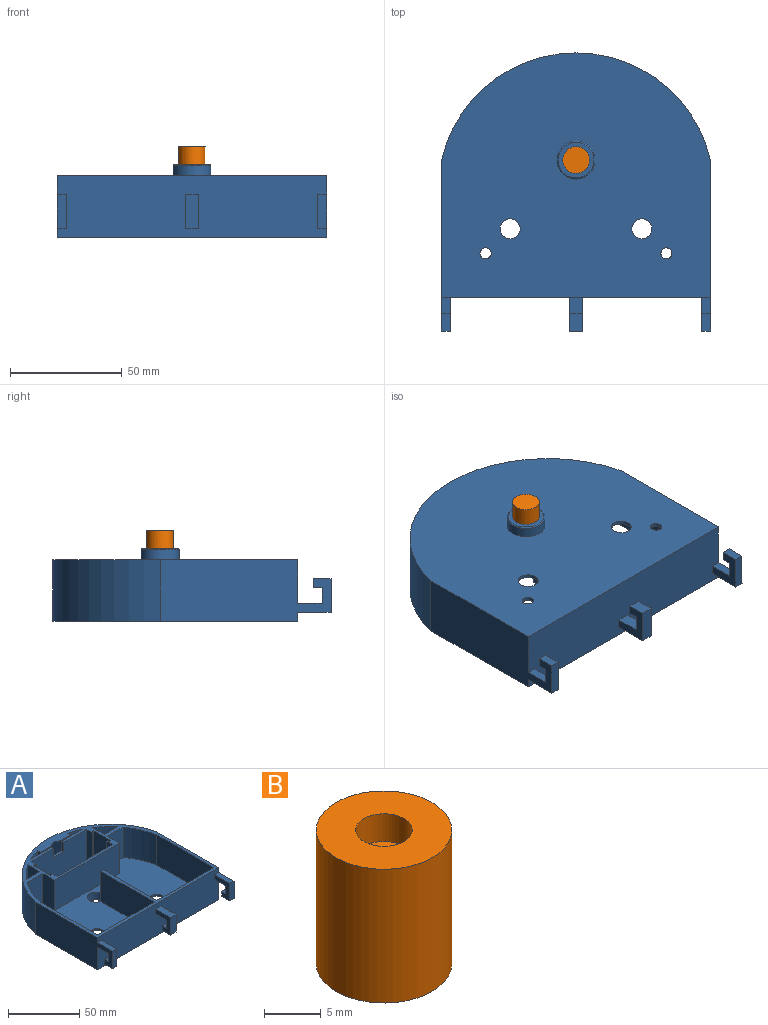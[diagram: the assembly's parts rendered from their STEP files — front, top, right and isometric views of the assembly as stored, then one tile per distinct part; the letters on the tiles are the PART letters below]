
ASSEMBLY  parts=2 mates=1
PART A: 95 faces, bbox 120.5x124.6x32.5 mm
  f0: plane 120.5x109.55mm, normal (0,0,1), area 1790.4mm2, adj f1,f2,f3,f5,f6,f8,f9,f12
  f1: plane 55x26mm, normal (0,-1,0), area 1350mm2, adj f0,f3,f4,f5,f6,f7,f85
  f2: plane 55x26mm, normal (0,1,0), area 1430mm2, adj f0,f3,f4,f85
  f3: plane 26x26mm, normal (1,0,0), area 359.2mm2, adj f0,f1,f2,f4,f76,f77,f78
  f4: plane 55x26mm, normal (0,0,1), area 1430mm2, adj f1,f2,f3,f85
  f5: plane 8x2mm, normal (1,0,0), area 16mm2, adj f0,f1,f7,f68
  f6: plane 8x2mm, normal (-1,0,0), area 16mm2, adj f0,f1,f7,f68
  f7: plane 10x2mm, normal (0,0,1), area 20mm2, adj f1,f5,f6,f68
  f8: cylinder r=58.84mm len=26mm, axis (0,0,1), area 462.6mm2, adj f0,f11,f13,f73
  f9: cylinder r=58.84mm len=26mm, axis (0,0,1), area 462.6mm2, adj f0,f10,f12,f74
  f10: plane 13.25x11.77mm, normal (0,0,1), area 85.9mm2, adj f9,f12,f74
  f11: plane 13.25x11.77mm, normal (0,0,1), area 85.9mm2, adj f8,f13,f73
  f12: plane 26x11.77mm, normal (-1,0,0), area 306mm2, adj f0,f9,f10,f74
  f13: plane 26x11.77mm, normal (1,0,0), area 306mm2, adj f0,f8,f11,f73
  f14: cylinder r=58.84mm len=51.77mm, axis (0,0,1), area 817.5mm2, adj f0,f16,f57,f58,f60,f68
  f15: cylinder r=58.84mm len=26mm, axis (0,0,1), area 666.6mm2, adj f0,f39,f54,f72
  f16: plane 51.77x6mm, normal (0,0,1), area 209.3mm2, adj f14,f68
  f17: cylinder r=58.84mm len=26mm, axis (0,0,1), area 666.6mm2, adj f0,f39,f40,f75
  f18: plane 53.18x26mm, normal (1,0,0), area 1382.7mm2, adj f0,f39,f55,f67
  f19: cylinder r=4.5mm len=9mm, axis (0,0,1), area 42.4mm2, adj f22,f39
  f20: plane 76.5x27.5mm, normal (-1,0,0), area 1811.2mm2, adj f0,f21,f22,f31,f32,f33,f35,f36
  f21: plane 120.5x27.5mm, normal (0,-1,0), area 3259.7mm2, adj f0,f20,f22,f25,f29,f30,f34,f37
  f22: plane 120.5x109.55mm, normal (0,0,-1), area 11331.1mm2, adj f19,f20,f21,f43,f44,f56,f64,f84
  f23: plane 7x5.5mm, normal (0,1,0), area 38.5mm2, adj f25,f28,f30,f45
  f24: plane 5.5x4mm, normal (0,1,0), area 22mm2, adj f25,f27,f28,f45
  f25: plane 15x15mm, normal (-1,0,0), area 120mm2, adj f21,f23,f24,f26,f27,f28,f29,f30
  f26: plane 15x5.5mm, normal (0,-1,0), area 82.5mm2, adj f25,f27,f29,f45
  f27: plane 8x5.5mm, normal (0,0,-1), area 44mm2, adj f24,f25,f26,f45
  f28: plane 5.5x4mm, normal (0,0,1), area 22mm2, adj f23,f24,f25,f45
  f29: plane 15x5.5mm, normal (0,0,1), area 82.5mm2, adj f21,f25,f26,f45
  f30: plane 11x5.5mm, normal (0,0,-1), area 60.5mm2, adj f21,f23,f25,f45
  f31: plane 7x4mm, normal (0,1,0), area 28mm2, adj f20,f34,f36,f38
  f32: plane 4x4mm, normal (0,1,0), area 16mm2, adj f20,f34,f35,f36
  f33: plane 15x4mm, normal (0,-1,0), area 60mm2, adj f20,f34,f35,f37
  f34: plane 15x15mm, normal (1,0,0), area 120mm2, adj f21,f31,f32,f33,f35,f36,f37,f38
  f35: plane 8x4mm, normal (0,0,-1), area 32mm2, adj f20,f32,f33,f34
  f36: plane 4x4mm, normal (0,0,1), area 16mm2, adj f20,f31,f32,f34
  f37: plane 15x4mm, normal (0,0,1), area 60mm2, adj f20,f21,f33,f34
  f38: plane 11x4mm, normal (0,0,-1), area 44mm2, adj f20,f21,f31,f34
  f39: plane 115.5x79.82mm, normal (0,0,1), area 7863.9mm2, adj f15,f17,f18,f19,f40,f41,f42,f43
  f40: plane 56.5x26mm, normal (1,0,0), area 1469mm2, adj f0,f17,f39,f41
  f41: plane 56.5x26mm, normal (0,1,0), area 1469mm2, adj f0,f39,f40,f42
  f42: plane 53.18x26mm, normal (-1,0,0), area 1382.7mm2, adj f0,f39,f41,f67
  f43: cylinder r=4.5mm len=9mm, axis (0,0,1), area 42.4mm2, adj f22,f39
  f44: plane 76.5x27.5mm, normal (1,0,0), area 1811.2mm2, adj f0,f21,f22,f46,f47,f48,f50,f51
  f45: plane 15x15mm, normal (1,0,0), area 120mm2, adj f21,f23,f24,f26,f27,f28,f29,f30
  f46: plane 7x4mm, normal (0,1,0), area 28mm2, adj f44,f49,f51,f53
  f47: plane 4x4mm, normal (0,1,0), area 16mm2, adj f44,f49,f50,f51
  f48: plane 15x4mm, normal (0,-1,0), area 60mm2, adj f44,f49,f50,f52
  f49: plane 15x15mm, normal (-1,0,0), area 120mm2, adj f21,f46,f47,f48,f50,f51,f52,f53
  f50: plane 8x4mm, normal (0,0,-1), area 32mm2, adj f44,f47,f48,f49
  f51: plane 4x4mm, normal (0,0,1), area 16mm2, adj f44,f46,f47,f49
  f52: plane 15x4mm, normal (0,0,1), area 60mm2, adj f21,f44,f48,f49
  f53: plane 11x4mm, normal (0,0,-1), area 44mm2, adj f21,f44,f46,f49
  f54: plane 56.5x26mm, normal (-1,0,0), area 1469mm2, adj f0,f15,f39,f55
  f55: plane 56.5x26mm, normal (0,1,0), area 1469mm2, adj f0,f18,f39,f54
  f56: cylinder r=61.8mm len=120.5mm, axis (0,0,1), area 4576.5mm2, adj f0,f20,f22,f44
  f57: plane 30x5mm, normal (0,0,-1), area 130.7mm2, adj f14,f58,f59,f60
  f58: plane 19x3.06mm, normal (-1,0,0), area 58.1mm2, adj f0,f14,f57,f59
  f59: plane 30x19mm, normal (0,-1,0), area 285.2mm2, adj f0,f57,f58,f60,f61,f62,f63
  f60: plane 19x3.06mm, normal (1,0,0), area 58.1mm2, adj f0,f14,f57,f59
  f61: plane 15x13.99mm, normal (-0.43,-0.86,-0.26), area 164.8mm2, adj f0,f59,f62,f63
  f62: plane 15x13.99mm, normal (0.43,-0.86,-0.26), area 164.8mm2, adj f0,f59,f61,f63
  f63: plane 27.97x6.99mm, normal (0,0,1), area 97.8mm2, adj f59,f61,f62
  f64: cylinder r=8.5mm len=17mm, axis (0,0,1), area 240.3mm2, adj f22,f66
  f65: plane 16x16mm, normal (0,0,-1), area 88mm2, adj f66,f67
  f66: torus R=8mm, axis (0,0,1), area 41mm2, adj f64,f65
  f67: cylinder r=6mm len=32.5mm, axis (0,0,1), area 310.5mm2, adj f0,f18,f39,f42,f65
  f68: plane 51.77x26mm, normal (0,1,0), area 1266.1mm2, adj f0,f5,f6,f7,f14,f16
  f69: plane 26x11.77mm, normal (-1,0,0), area 306mm2, adj f0,f39,f70,f75
  f70: plane 64x26mm, normal (0,-1,0), area 1664mm2, adj f0,f39,f69,f71
  f71: plane 26x11.77mm, normal (1,0,0), area 306mm2, adj f0,f39,f70,f72
  f72: plane 26x15.59mm, normal (0,-1,0), area 405.3mm2, adj f0,f15,f39,f71
  f73: plane 26x13.25mm, normal (0,1,0), area 344.6mm2, adj f0,f8,f11,f13
  f74: plane 26x13.25mm, normal (0,1,0), area 344.6mm2, adj f0,f9,f10,f12
  f75: plane 26x15.59mm, normal (0,-1,0), area 405.3mm2, adj f0,f17,f39,f69
  f76: plane 22x1.4mm, normal (0,-1,0), area 30.8mm2, adj f0,f3,f78,f82
  f77: plane 22x1.4mm, normal (0,1,0), area 30.8mm2, adj f0,f3,f78,f81
  f78: plane 17x2.5mm, normal (0,0,1), area 38.9mm2, adj f3,f76,f77,f79,f80,f81,f82,f83
  f79: plane 22x17mm, normal (1,0,0), area 374mm2, adj f0,f78,f80,f83
  f80: plane 22x1.1mm, normal (0,1,0), area 24.2mm2, adj f0,f78,f79,f81
  f81: plane 22x1.3mm, normal (-1,0,0), area 28.6mm2, adj f0,f77,f78,f80
  f82: plane 22x1.3mm, normal (-1,0,0), area 28.6mm2, adj f0,f76,f78,f83
  f83: plane 22x1.1mm, normal (0,-1,0), area 24.2mm2, adj f0,f78,f79,f82
  f84: cylinder r=2.5mm len=5mm, axis (0,0,1), area 23.6mm2, adj f22,f39
  f85: plane 26x26mm, normal (-1,0,0), area 359.2mm2, adj f0,f1,f2,f4,f86,f87,f89
  f86: plane 22x1.4mm, normal (0,-1,0), area 30.8mm2, adj f0,f85,f89,f93
  f87: plane 22x1.4mm, normal (0,1,0), area 30.8mm2, adj f0,f85,f89,f91
  f88: plane 22x17mm, normal (-1,0,0), area 374mm2, adj f0,f89,f90,f92
  f89: plane 17x2.5mm, normal (0,0,1), area 38.9mm2, adj f85,f86,f87,f88,f90,f91,f92,f93
  f90: plane 22x1.1mm, normal (0,1,0), area 24.2mm2, adj f0,f88,f89,f91
  f91: plane 22x1.3mm, normal (1,0,0), area 28.6mm2, adj f0,f87,f89,f90
  f92: plane 22x1.1mm, normal (0,-1,0), area 24.2mm2, adj f0,f88,f89,f93
  f93: plane 22x1.3mm, normal (1,0,0), area 28.6mm2, adj f0,f86,f89,f92
  f94: cylinder r=2.5mm len=5mm, axis (0,0,1), area 23.6mm2, adj f22,f39
PART B: 5 faces, bbox 12x12x14.5 mm
  f0: cylinder r=6mm len=14.5mm, axis (0,0,1), area 546.6mm2, adj f1,f2
  f1: plane 12x12mm, normal (0,0,-1), area 113.1mm2, adj f0
  f2: plane 12x12mm, normal (0,0,1), area 93.5mm2, adj f0,f3
  f3: cylinder r=2.5mm len=5mm, axis (0,0,1), area 47.1mm2, adj f2,f4
  f4: plane 5x5mm, normal (0,0,1), area 19.6mm2, adj f3
PLACE A rot(axis=(0,1,0),180deg) t=(101.02,-12.76,-38.51)mm fixed
PLACE B rot(axis=(0,1,0),180deg) t=(101.02,-12.76,-45.01)mm
MATE fastened B.f0 <-> A.f64  axis (0,0,-1) through (71.52,18.04,-12.51)mm
